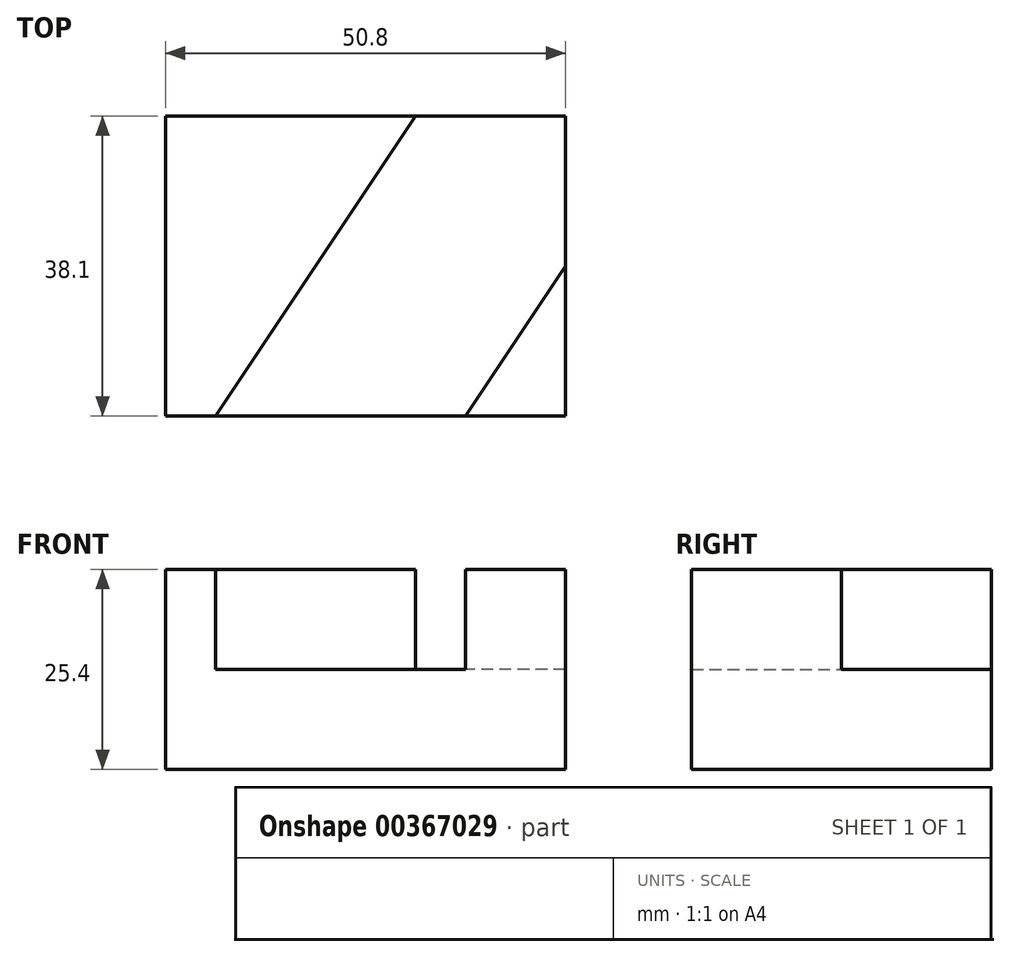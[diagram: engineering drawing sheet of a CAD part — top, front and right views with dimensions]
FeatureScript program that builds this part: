
annotation { "Feature Type Name" : "Feature", "Feature Type Description" : "" }
export const myFeature = defineFeature(function(context is Context, id is Id, definition is map)
    precondition{}
    {
        {
            var Q0;
            Q0=qCreatedBy(makeId("Right.planeOp"),FACE);
            var sketch = newSketch(context, id + "F0", { "sketchPlane" : qUnion([Q0])});
            skLineSegment(sketch, "E0", {"start": v(0, 0) * mm, "end": v(38.1, 0) * mm});
            skLineSegment(sketch, "E1", {"start": v(38.1, 0) * mm, "end": v(38.1, 25.4) * mm});
            skLineSegment(sketch, "E2", {"start": v(38.1, 25.4) * mm, "end": v(0, 25.4) * mm});
            skLineSegment(sketch, "E3", {"start": v(0, 25.4) * mm, "end": v(0, 0) * mm});
            skSolve(sketch);
        }
        {
            var Q0;
            Q0 = qSketchRegion(id + "F0", true);
            extrude(context, id + "F1", {"entities" : qUnion([Q0]), "depth" : 50.8 * mm});
        }
        {
            var Q0;
            Q0=makeQuery(id+"F1.opExtrude","SWEPT_FACE",FACE,{"disambiguationData":[OSD([sQuery(id+"F0.wireOp",EDGE,"E2")])]});
            var sketch = newSketch(context, id + "F2", { "sketchPlane" : qUnion([Q0])});
            skLineSegment(sketch, "E4", {"start": v(6.35, 0) * mm, "end": v(31.75, 38.1) * mm});
            skLineSegment(sketch, "E5", {"start": v(31.75, 38.1) * mm, "end": v(50.8, 38.1) * mm});
            skLineSegment(sketch, "E6", {"start": v(50.8, 38.1) * mm, "end": v(50.8, 19.05) * mm});
            skLineSegment(sketch, "E7", {"start": v(50.8, 19.05) * mm, "end": v(38.1, 0) * mm});
            skLineSegment(sketch, "E8", {"start": v(38.1, 0) * mm, "end": v(6.35, 0) * mm});
            skLineSegment(sketch, "E9", {"start": v(6.35, 0) * mm, "end": v(38.1, 0) * mm});
            skSolve(sketch);
        }
        {
            var Q0;
            Q0=makeQuery(id+"F2.imprint","IMPRINT",FACE,{"disambiguationData":[TD([[makeQuery(id+"F2.imprint","IMPRINT",EDGE,{"derivedFrom":sQuery(id+"F2.wireOp",EDGE,"E4")}),-1.0]])]});
            extrude(context, id + "F3", {"entities" : qUnion([Q0]), "operationType" : NewBodyOperationType.REMOVE, "depth" : 25.4 * mm});
        }
        {
            var Q0;
            Q0=makeQuery(id+"F2.imprint","IMPRINT",FACE,{"disambiguationData":[TD([[makeQuery(id+"F2.imprint","IMPRINT",EDGE,{"derivedFrom":sQuery(id+"F2.wireOp",EDGE,"E4")}),-1.0]])]});
            extrude(context, id + "F4", {"entities" : qUnion([Q0]), "operationType" : NewBodyOperationType.REMOVE, "oppositeDirection" : true, "depth" : 12.7 * mm});
        }
    });
